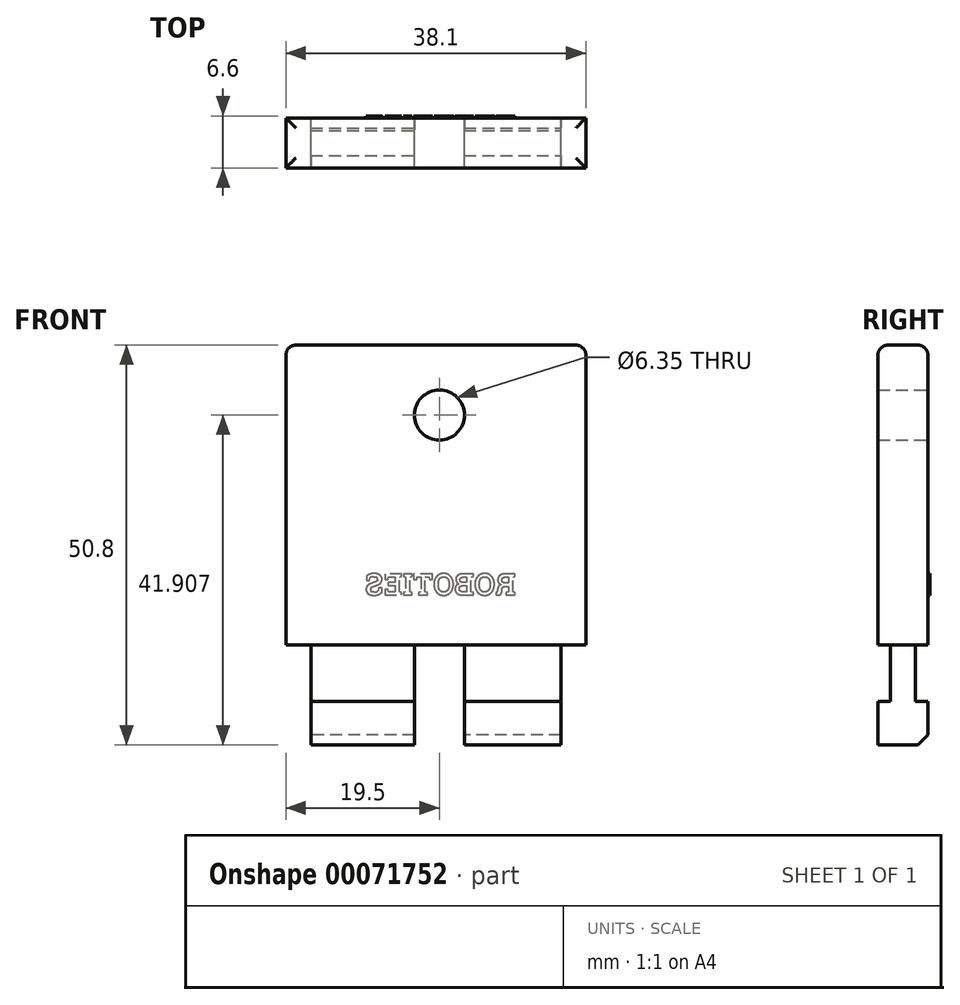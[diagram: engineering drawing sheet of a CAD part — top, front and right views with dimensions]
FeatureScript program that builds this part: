
annotation { "Feature Type Name" : "Feature", "Feature Type Description" : "" }
export const myFeature = defineFeature(function(context is Context, id is Id, definition is map)
    precondition{}
    {
        {
            var Q0;
            Q0=qCreatedBy(makeId("Front.planeOp"),FACE);
            var sketch = newSketch(context, id + "F0", { "sketchPlane" : qUnion([Q0])});
            skLineSegment(sketch, "E0.bottom", {"start": v(-19.5, 43.19) * mm, "end": v(18.6, 43.19) * mm});
            skLineSegment(sketch, "E0.top", {"start": v(-19.5, -7.61) * mm, "end": v(18.6, -7.61) * mm});
            skLineSegment(sketch, "E0.left", {"start": v(-19.5, 43.19) * mm, "end": v(-19.5, -7.61) * mm});
            skLineSegment(sketch, "E0.right", {"start": v(18.6, 43.19) * mm, "end": v(18.6, -7.61) * mm});
            skSolve(sketch);
        }
        {
            var Q0;
            Q0 = qSketchRegion(id + "F0", true);
            extrude(context, id + "F1", {"entities" : qUnion([Q0]), "depth" : 6.35 * mm});
        }
        {
            var Q0;
            Q0=makeQuery(id+"F1.opExtrude","CAP_FACE",FACE,{"disambiguationData":[OSD([sQuery(id+"F0.wireOp",EDGE,"E0.bottom"),sQuery(id+"F0.wireOp",EDGE,"E0.top"),sQuery(id+"F0.wireOp",EDGE,"E0.left"),sQuery(id+"F0.wireOp",EDGE,"E0.right")])],"isStart":true});
            var sketch = newSketch(context, id + "F2", { "sketchPlane" : qUnion([Q0])});
            skLineSegment(sketch, "E1", {"start": v(0, -7.61) * mm, "end": v(0, 43.19) * mm, "construction": true});
            skPoint(sketch, "E1.startSnap0", {"position": v(0.45, -7.61) * mm});
            skLineSegment(sketch, "E2", {"start": v(-18.6, 34.3) * mm, "end": v(19.5, 34.3) * mm, "construction": true});
            skCircle(sketch, "E3", {"center": v(0, 34.3) * mm, "radius": 3.18 * mm});
            skSolve(sketch);
        }
        {
            var Q0;
            Q0 = qSketchRegion(id + "F2", true);
            extrude(context, id + "F3", {"entities" : qUnion([Q0]), "operationType" : NewBodyOperationType.REMOVE, "endBound" : BoundingType.THROUGH_ALL, "oppositeDirection" : true, "depth" : 25.4 * mm});
        }
        {
            var Q0;
            Q0=makeQuery(id+"F1.opExtrude","CAP_FACE",FACE,{"disambiguationData":[OSD([sQuery(id+"F0.wireOp",EDGE,"E0.bottom"),sQuery(id+"F0.wireOp",EDGE,"E0.top"),sQuery(id+"F0.wireOp",EDGE,"E0.left"),sQuery(id+"F0.wireOp",EDGE,"E0.right")])],"isStart":true});
            var sketch = newSketch(context, id + "F4", { "sketchPlane" : qUnion([Q0])});
            skLineSegment(sketch, "E4.bottom", {"start": v(-18.6, 5.09) * mm, "end": v(-15.43, 5.09) * mm});
            skLineSegment(sketch, "E4.top", {"start": v(-18.6, -7.61) * mm, "end": v(-15.43, -7.61) * mm});
            skLineSegment(sketch, "E4.left", {"start": v(-18.6, 5.09) * mm, "end": v(-18.6, -7.61) * mm});
            skLineSegment(sketch, "E4.right", {"start": v(-15.43, 5.09) * mm, "end": v(-15.43, -7.61) * mm});
            skLineSegment(sketch, "E5.bottom", {"start": v(19.5, 5.09) * mm, "end": v(16.32, 5.09) * mm});
            skLineSegment(sketch, "E5.top", {"start": v(19.5, -7.61) * mm, "end": v(16.32, -7.61) * mm});
            skLineSegment(sketch, "E5.left", {"start": v(19.5, 5.09) * mm, "end": v(19.5, -7.61) * mm});
            skLineSegment(sketch, "E5.right", {"start": v(16.32, 5.09) * mm, "end": v(16.32, -7.61) * mm});
            skSolve(sketch);
        }
        {
            var Q0;
            Q0 = qSketchRegion(id + "F4", true);
            extrude(context, id + "F5", {"entities" : qUnion([Q0]), "operationType" : NewBodyOperationType.REMOVE, "endBound" : BoundingType.THROUGH_ALL, "oppositeDirection" : true, "depth" : 25.4 * mm});
        }
        {
            var Q0;
            Q0=makeQuery(id+"F1.opExtrude","CAP_FACE",FACE,{"disambiguationData":[OSD([sQuery(id+"F0.wireOp",EDGE,"E0.bottom"),sQuery(id+"F0.wireOp",EDGE,"E0.top"),sQuery(id+"F0.wireOp",EDGE,"E0.left"),sQuery(id+"F0.wireOp",EDGE,"E0.right")])],"isStart":true});
            var sketch = newSketch(context, id + "F6", { "sketchPlane" : qUnion([Q0])});
            skLineSegment(sketch, "E6.bottom", {"start": v(-3.17, -7.61) * mm, "end": v(3.18, -7.61) * mm});
            skLineSegment(sketch, "E6.top", {"start": v(-3.17, 5.09) * mm, "end": v(3.18, 5.09) * mm});
            skLineSegment(sketch, "E6.left", {"start": v(-3.17, -7.61) * mm, "end": v(-3.17, 5.09) * mm});
            skLineSegment(sketch, "E6.right", {"start": v(3.18, -7.61) * mm, "end": v(3.18, 5.09) * mm});
            skLineSegment(sketch, "E7", {"start": v(0, 43.19) * mm, "end": v(0, -7.61) * mm, "construction": true});
            skSolve(sketch);
        }
        {
            var Q0;
            Q0 = qSketchRegion(id + "F6", true);
            extrude(context, id + "F7", {"entities" : qUnion([Q0]), "operationType" : NewBodyOperationType.REMOVE, "endBound" : BoundingType.THROUGH_ALL, "oppositeDirection" : true, "depth" : 25.4 * mm});
        }
        {
            var Q0;
            Q0=makeQuery(id+"F1.opExtrude","CAP_FACE",FACE,{"disambiguationData":[OSD([sQuery(id+"F0.wireOp",EDGE,"E0.bottom"),sQuery(id+"F0.wireOp",EDGE,"E0.top"),sQuery(id+"F0.wireOp",EDGE,"E0.left"),sQuery(id+"F0.wireOp",EDGE,"E0.right")])],"isStart":true});
            var sketch = newSketch(context, id + "F8", { "sketchPlane" : qUnion([Q0])});
            skText(sketch, "E8", { "text": "ROBOTIES", "fontName": "RobotoSlab-Bold.ttf"});
            const initialGuessF8  = {"E8": [-0.00971, 0.01143, 1, 0, 0.00274]};
            skSetInitialGuess(sketch, initialGuessF8);
            skSolve(sketch);
        }
        {
            var Q0;
            Q0 = qSketchRegion(id + "F8", true);
            extrude(context, id + "F9", {"entities" : qUnion([Q0]), "operationType" : NewBodyOperationType.ADD, "depth" : 0.25 * mm});
        }
        {
            var Q0;
            Q0=makeQuery(id+"F1.opExtrude","CAP_EDGE",EDGE,{"disambiguationData":[OSD([sQuery(id+"F0.wireOp",EDGE,"E0.bottom")])],"isStart":false});
            var Q1;
            Q1=makeQuery(id+"F1.opExtrude","SWEPT_EDGE",EDGE,{"disambiguationData":[OSD([sQuery(id+"F0.wireOp",EDGE,"E0.bottom"),sQuery(id+"F0.wireOp",EDGE,"E0.right")])]});
            var Q2;
            Q2=makeQuery(id+"F1.opExtrude","CAP_EDGE",EDGE,{"disambiguationData":[OSD([sQuery(id+"F0.wireOp",EDGE,"E0.bottom")])],"isStart":true});
            var Q3;
            Q3=makeQuery(id+"F1.opExtrude","SWEPT_EDGE",EDGE,{"disambiguationData":[OSD([sQuery(id+"F0.wireOp",EDGE,"E0.bottom"),sQuery(id+"F0.wireOp",EDGE,"E0.left")])]});
            fillet(context, id + "F10", {"entities" : qUnion([Q0, Q1, Q2, Q3]), "radius" : 1.27 * mm, "tangentPropagation" : true, "allowEdgeOverflow" : false});
        }
        {
            var Q0;
            {var subQ0=sQuery(id+"F0.wireOp",EDGE,"E0.top");Q0=makeQuery(id+"F7.boolean.opBoolean","SPLIT",EDGE,{"disambiguationData":[TD([makeQuery(id+"F5.boolean.opBoolean","COPY",FACE,{"derivedFrom":makeQuery(id+"F5.opExtrude","SWEPT_FACE",FACE,{"disambiguationData":[OSD([sQuery(id+"F4.wireOp",EDGE,"E4.right")])]})})])],"derivedFrom":makeQuery(id+"F1.opExtrude","CAP_EDGE",EDGE,{"disambiguationData":[OSD([subQ0])],"isStart":true})});}
            var Q1;
            {var subQ0=sQuery(id+"F0.wireOp",EDGE,"E0.top");Q1=makeQuery(id+"F7.boolean.opBoolean","SPLIT",EDGE,{"disambiguationData":[TD([makeQuery(id+"F5.boolean.opBoolean","COPY",FACE,{"derivedFrom":makeQuery(id+"F5.opExtrude","SWEPT_FACE",FACE,{"disambiguationData":[OSD([sQuery(id+"F4.wireOp",EDGE,"E5.right")])]})})])],"derivedFrom":makeQuery(id+"F1.opExtrude","CAP_EDGE",EDGE,{"disambiguationData":[OSD([subQ0])],"isStart":true})});}
            chamfer(context, id + "F11", {"entities" : qUnion([Q0, Q1]), "width" : 1.27 * mm, "tangentPropagation" : true});
        }
        {
            var Q0;
            Q0=makeQuery(id+"F5.boolean.opBoolean","COPY",FACE,{"derivedFrom":makeQuery(id+"F5.opExtrude","SWEPT_FACE",FACE,{"disambiguationData":[OSD([sQuery(id+"F4.wireOp",EDGE,"E4.right")])]})});
            var sketch = newSketch(context, id + "F12", { "sketchPlane" : qUnion([Q0])});
            skLineSegment(sketch, "E9", {"start": v(0, 5.09) * mm, "end": v(-6.35, 5.09) * mm, "construction": true});
            skLineSegment(sketch, "E10.bottom", {"start": v(-4.76, 5.09) * mm, "end": v(-6.35, 5.09) * mm});
            skLineSegment(sketch, "E10.top", {"start": v(-4.76, -2.1) * mm, "end": v(-6.35, -2.1) * mm});
            skLineSegment(sketch, "E10.left", {"start": v(-4.76, 5.09) * mm, "end": v(-4.76, -2.1) * mm});
            skLineSegment(sketch, "E10.right", {"start": v(-6.35, 5.09) * mm, "end": v(-6.35, -2.1) * mm});
            skLineSegment(sketch, "E11", {"start": v(-3.18, 5.09) * mm, "end": v(-3.17, -7.61) * mm, "construction": true});
            skLineSegment(sketch, "E12.MirrorCS", {"start": v(-1.59, -2.1) * mm, "end": v(0, -2.1) * mm});
            skLineSegment(sketch, "E13.MirrorCS", {"start": v(-1.59, 5.09) * mm, "end": v(-1.59, -2.1) * mm});
            skLineSegment(sketch, "E14.MirrorCS", {"start": v(0, 5.09) * mm, "end": v(0, -2.1) * mm});
            skLineSegment(sketch, "E15", {"start": v(-1.59, 5.09) * mm, "end": v(0, 5.09) * mm});
            skSolve(sketch);
        }
        {
            var Q0;
            Q0 = qSketchRegion(id + "F12", true);
            extrude(context, id + "F13", {"entities" : qUnion([Q0]), "operationType" : NewBodyOperationType.REMOVE, "endBound" : BoundingType.THROUGH_ALL, "oppositeDirection" : true, "depth" : 25.4 * mm});
        }
    });
